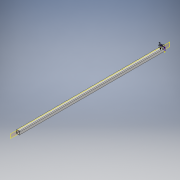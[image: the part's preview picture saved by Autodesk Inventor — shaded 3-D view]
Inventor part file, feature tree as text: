
AUTODESK INVENTOR PART (.ipt)
format: ipt  version: 2019 (Build 230136000, 136)  size: 135,680 bytes
history: native  units: in
note: dims shown in document units (in); Inventor stores cm internally (conversion verified against a paired STEP export)
features: extrude x2, sketch x2, other x2, pattern_linear x1, plane x1
ambient origin geometry x8: Origin, YZ Plane, XZ Plane, XY Plane, X Axis, Y Axis, Z Axis, Center Point
bodies: Solid1 (feature_tree)
feature tree (8):
  extrude  "Extrusion1"  Depth=1.9685in
  extrude  "Extrusion2"  Depth=0.1969in
  pattern_linear  "Rectangular Pattern1"  Count1=200 Spacing1=0.0in
  plane  "Work Plane1"
  sketch  "Sketch1"  dims[d0=1.9685in d1=1.9685in]
  sketch  "Sketch2"  dims[d2=0.315in d3=0.1969in d4=78.7402in d5=0.0in d6=1.1811in d7=3.937in d8=1.5748in d10=17.7165in d11=0.3937in d13=0.3937in d22=0.2362in d23=236.2205in d24=0.0in d25=0.7874in d27=17.7165in]
  other  "Work Axis1"
  other  "Work Axis2"
